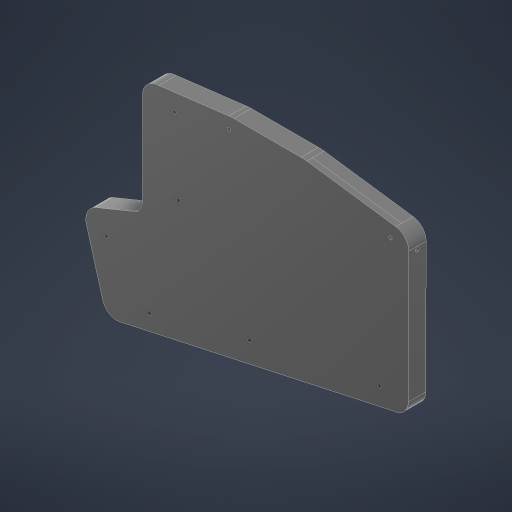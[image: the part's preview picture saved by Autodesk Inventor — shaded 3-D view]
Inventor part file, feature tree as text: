
AUTODESK INVENTOR PART (.ipt)
format: ipt  version: 2024.3 (Build 283343000, 343)  size: 448,512 bytes
history: native  units: in
note: dims shown in document units (in); Inventor stores cm internally (conversion verified against a paired STEP export)
features: extrude x6, sketch x6, projected_geometry x5, other x3, reference x2
ambient origin geometry x8: Origin, YZ Plane, XZ Plane, XY Plane, X Axis, Y Axis, Z Axis, Center Point
bodies: Solid1 (feature_tree)
feature tree (22):
  extrude  "Extrusion1"  Depth=0.125in TaperAngle=0.0deg
  extrude  "Extrusion2"  Depth=0.25in TaperAngle=0.0deg
  extrude  "Extrusion3"  Depth=0.125in
  sketch  "Sketch4"  dims[d8=0.0312in d9=0.0312in]
  sketch  "Sketch5"  dims[d10=0.0312in d11=0.0312in]
  extrude  "Extrusion4"  Depth=0.0312in
  extrude  "Extrusion5"  Depth=0.0312in
  extrude  "Extrusion6"  Depth=0.25in
  sketch  "Sketch1"  dims[d0=0.125in d1=0.125in d2=0.0in]
  reference  "Reference1"
  sketch  "Sketch2"  dims[d3=0.12in d4=0.25in d5=0.0in]
  projected_geometry  "Projected Loop1"
  sketch  "Sketch3"  dims[d6=0.125in d7=0.0312in]
  reference  "Reference2"
  projected_geometry  "Projected Loop2"
  projected_geometry  "Projected Loop3"
  projected_geometry  "Projected Loop4"
  sketch  "Sketch6"  dims[d12=0.0312in d13=0.0312in d14=0.0312in d15=0.125in d16=0.125in d17=0.125in d18=0.125in d19=0.125in d20=0.125in d21=0.125in d22=0.125in d23=0.125in d24=0.125in d25=0.125in d26=0.125in d27=0.125in d28=0.125in d29=0.125in d30=0.0in d31=0.0938in d32=0.0625in d33=0.1875in d34=0.0938in d35=0.1875in d36=0.0625in d37=0.0938in d38=0.1875in d39=0.3125in d40=0.25in d41=0.0in d42=0.25in d43=0.0in d44=0.25in d45=0.0in d46=0.003in d47=0.003in d48=0.003in d49=0.003in d50=0.003in d51=0.003in d52=0.003in d53=0.003in]
  projected_geometry  "Projected Loop5"
  other  "<userpath>\Documents\GitHub\clackenPersonal\Case Cad\Main Case Assembly.iam"
  other  "Main Case Assembly.iam"
  other  "Split V2:1"
